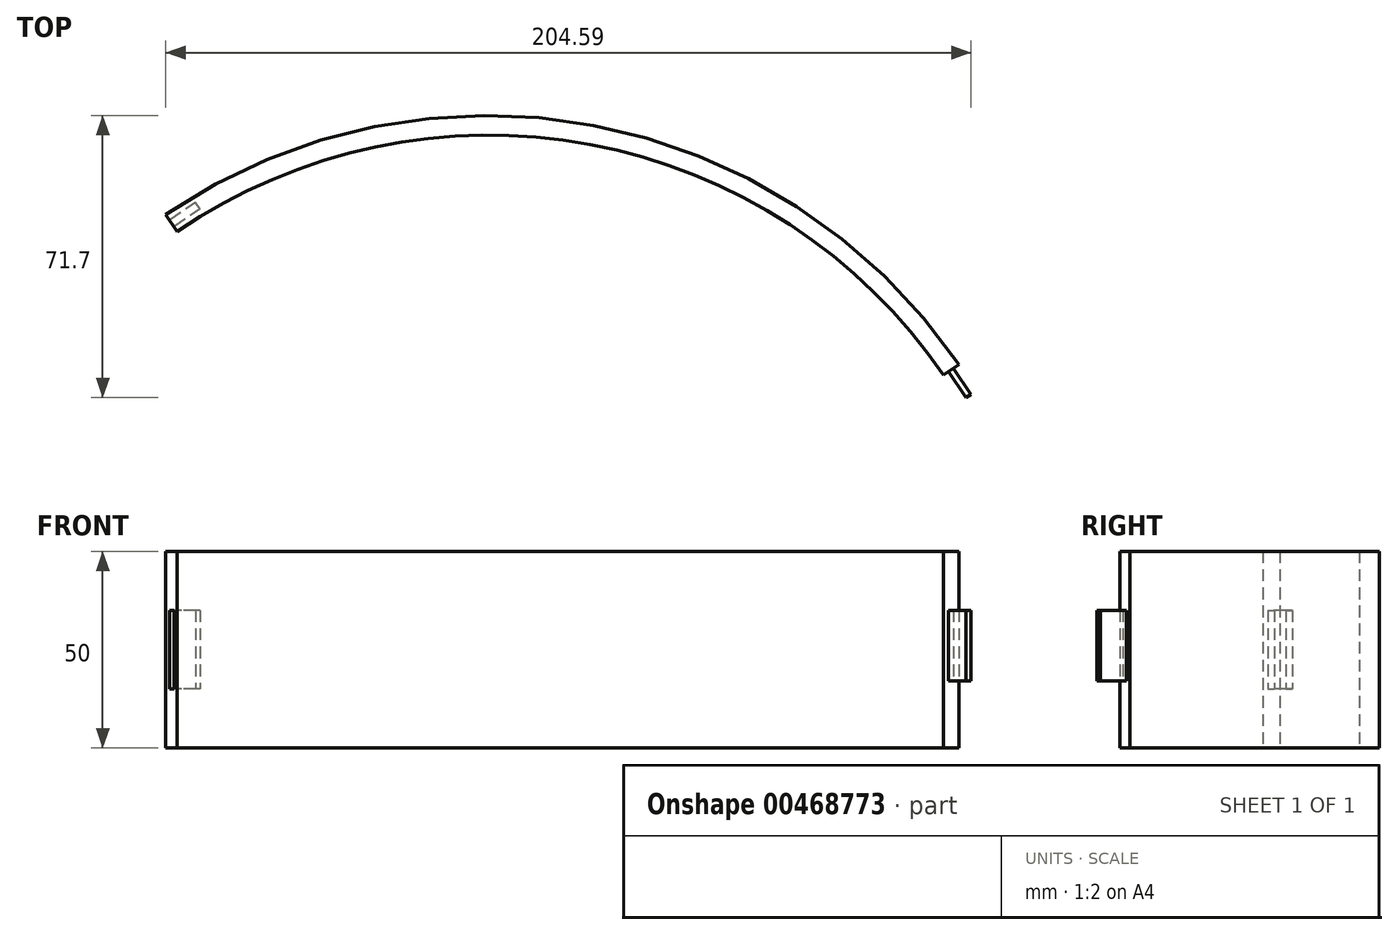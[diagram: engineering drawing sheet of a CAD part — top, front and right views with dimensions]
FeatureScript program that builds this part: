
annotation { "Feature Type Name" : "Feature", "Feature Type Description" : "" }
export const myFeature = defineFeature(function(context is Context, id is Id, definition is map)
    precondition{}
    {
        {
            var Q0;
            Q0=qCreatedBy(makeId("Top.planeOp"),FACE);
            var sketch = newSketch(context, id + "F0", { "sketchPlane" : qUnion([Q0])});
            skArc(sketch, "E0", {"start": v(119.78, 81.71) * mm, "mid": v(26.92, 142.48) * mm, "end": v(-81.71, 119.78) * mm});
            skLineSegment(sketch, "E1", {"start": v(119.78, 81.71) * mm, "end": v(0, 0) * mm});
            skLineSegment(sketch, "E2", {"start": v(0, 0) * mm, "end": v(-81.71, 119.78) * mm});
            skArc(sketch, "E3", {"start": v(115.9, 79.06) * mm, "mid": v(26.1, 137.61) * mm, "end": v(-78.78, 115.48) * mm});
            skSolve(sketch);
        }
        {
            var Q0;
            {var subQ0=sQuery(id+"F0.wireOp",EDGE,"E0");Q0=makeQuery(id+"F0.imprint","IMPRINT",FACE,{"disambiguationData":[TD([[makeQuery(id+"F0.imprint","IMPRINT",EDGE,{"derivedFrom":subQ0}),1.0]])]});}
            extrude(context, id + "F1", {"entities" : qUnion([Q0]), "depth" : 50 * mm});
        }
        {
            var Q0;
            Q0=makeQuery(id+"F1.opExtrude","SWEPT_FACE",FACE,{"disambiguationData":[OSD([sQuery(id+"F0.wireOp",EDGE,"E1")])]});
            cPlane(context, id + "F2", {"entities" : qUnion([Q0]), "cplaneType" : CPlaneType.OFFSET, "offset" : 0 * mm, "width" : 150 * mm, "height" : 150 * mm});
        }
        {
            var Q0;
            Q0=qCreatedBy(id+"F2.planeOp",FACE);
            var sketch = newSketch(context, id + "F3", { "sketchPlane" : qUnion([Q0])});
            skLineSegment(sketch, "E4.bottom", {"start": v(143.3, 35) * mm, "end": v(141.8, 35) * mm});
            skLineSegment(sketch, "E4.top", {"start": v(143.3, 17) * mm, "end": v(141.8, 17) * mm});
            skLineSegment(sketch, "E4.left", {"start": v(143.3, 35) * mm, "end": v(143.3, 17) * mm});
            skLineSegment(sketch, "E4.right", {"start": v(141.8, 35) * mm, "end": v(141.8, 17) * mm});
            skSolve(sketch);
        }
        {
            var Q0;
            Q0 = qSketchRegion(id + "F3", true);
            extrude(context, id + "F4", {"entities" : qUnion([Q0]), "operationType" : NewBodyOperationType.ADD, "depth" : 8 * mm});
        }
        {
            var Q0;
            Q0=makeQuery(id+"F1.opExtrude","SWEPT_FACE",FACE,{"disambiguationData":[OSD([sQuery(id+"F0.wireOp",EDGE,"E2")])]});
            cPlane(context, id + "F5", {"entities" : qUnion([Q0]), "cplaneType" : CPlaneType.OFFSET, "offset" : 0 * mm, "width" : 150 * mm, "height" : 150 * mm});
        }
        {
            var Q0;
            Q0=qCreatedBy(id+"F5.planeOp",FACE);
            var sketch = newSketch(context, id + "F6", { "sketchPlane" : qUnion([Q0])});
            skLineSegment(sketch, "E5.bottom", {"start": v(-141.3, 35) * mm, "end": v(-143.3, 35) * mm});
            skLineSegment(sketch, "E5.top", {"start": v(-141.3, 15) * mm, "end": v(-143.3, 15) * mm});
            skLineSegment(sketch, "E5.left", {"start": v(-141.3, 35) * mm, "end": v(-141.3, 15) * mm});
            skLineSegment(sketch, "E5.right", {"start": v(-143.3, 35) * mm, "end": v(-143.3, 15) * mm});
            skSolve(sketch);
        }
        {
            var Q0;
            Q0 = qSketchRegion(id + "F6", true);
            extrude(context, id + "F7", {"entities" : qUnion([Q0]), "operationType" : NewBodyOperationType.REMOVE, "oppositeDirection" : true, "depth" : 8 * mm});
        }
    });
